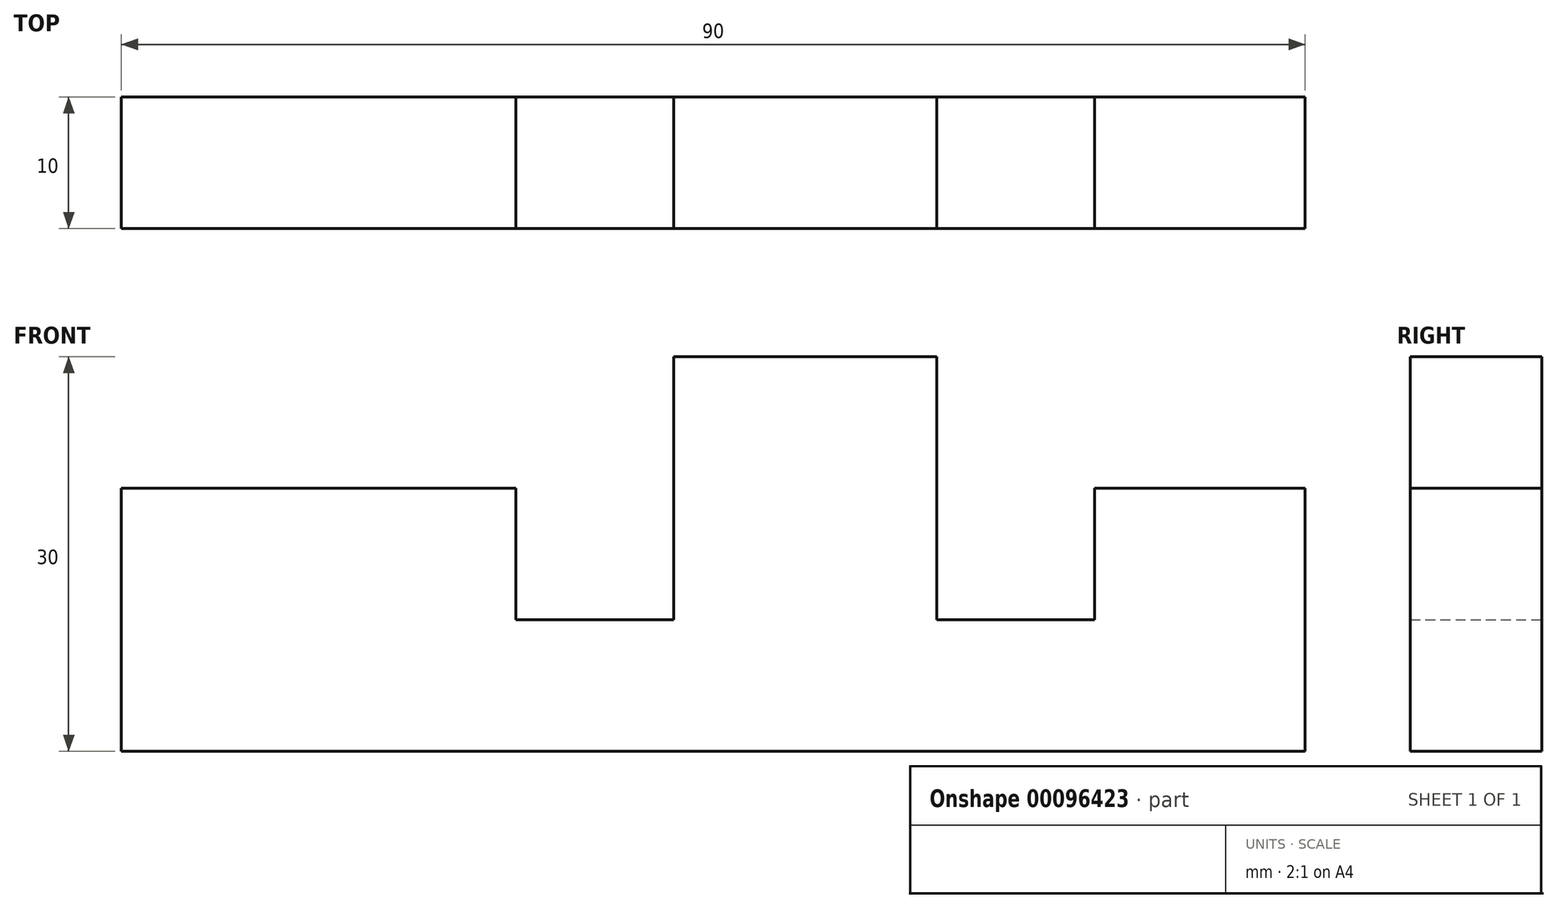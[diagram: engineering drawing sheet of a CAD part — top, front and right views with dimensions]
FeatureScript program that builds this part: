
annotation { "Feature Type Name" : "Feature", "Feature Type Description" : "" }
export const myFeature = defineFeature(function(context is Context, id is Id, definition is map)
    precondition{}
    {
        {
            var Q0;
            Q0=qCreatedBy(makeId("Front.planeOp"),FACE);
            var sketch = newSketch(context, id + "F0", { "sketchPlane" : qUnion([Q0])});
            skLineSegment(sketch, "E0.bottom", {"start": v(0, 0) * mm, "end": v(90, 0) * mm, "construction": true});
            skLineSegment(sketch, "E0.top", {"start": v(0, 20) * mm, "end": v(90, 20) * mm, "construction": true});
            skLineSegment(sketch, "E0.left", {"start": v(0, 0) * mm, "end": v(0, 20) * mm, "construction": true});
            skLineSegment(sketch, "E0.right", {"start": v(90, 0) * mm, "end": v(90, 20) * mm, "construction": true});
            skLineSegment(sketch, "E1", {"start": v(0, 0) * mm, "end": v(90, 0) * mm});
            skLineSegment(sketch, "E2", {"start": v(0, 0) * mm, "end": v(0, 20) * mm});
            skLineSegment(sketch, "E3", {"start": v(90, 0) * mm, "end": v(90, 20) * mm});
            skLineSegment(sketch, "E4", {"start": v(90, 20) * mm, "end": v(74, 20) * mm});
            skLineSegment(sketch, "E5", {"start": v(74, 20) * mm, "end": v(74, 10) * mm});
            skPoint(sketch, "E5.endSnap0", {"position": v(90, 10) * mm});
            skLineSegment(sketch, "E6", {"start": v(0, 20) * mm, "end": v(30, 20) * mm});
            skLineSegment(sketch, "E7", {"start": v(30, 20) * mm, "end": v(30, 10) * mm});
            skPoint(sketch, "E7.endSnap0", {"position": v(0, 10) * mm});
            skLineSegment(sketch, "E8", {"start": v(30, 10) * mm, "end": v(42, 10) * mm});
            skLineSegment(sketch, "E9", {"start": v(42, 10) * mm, "end": v(42, 30) * mm});
            skLineSegment(sketch, "E10", {"start": v(42, 30) * mm, "end": v(62, 30) * mm});
            skLineSegment(sketch, "E11", {"start": v(62, 30) * mm, "end": v(62, 10) * mm});
            skLineSegment(sketch, "E12", {"start": v(62, 10) * mm, "end": v(74, 10) * mm});
            skSolve(sketch);
        }
        {
            var Q0;
            Q0 = qSketchRegion(id + "F0", true);
            extrude(context, id + "F1", {"entities" : qUnion([Q0]), "endBound" : BoundingType.SYMMETRIC, "depth" : 10 * mm});
        }
    });
